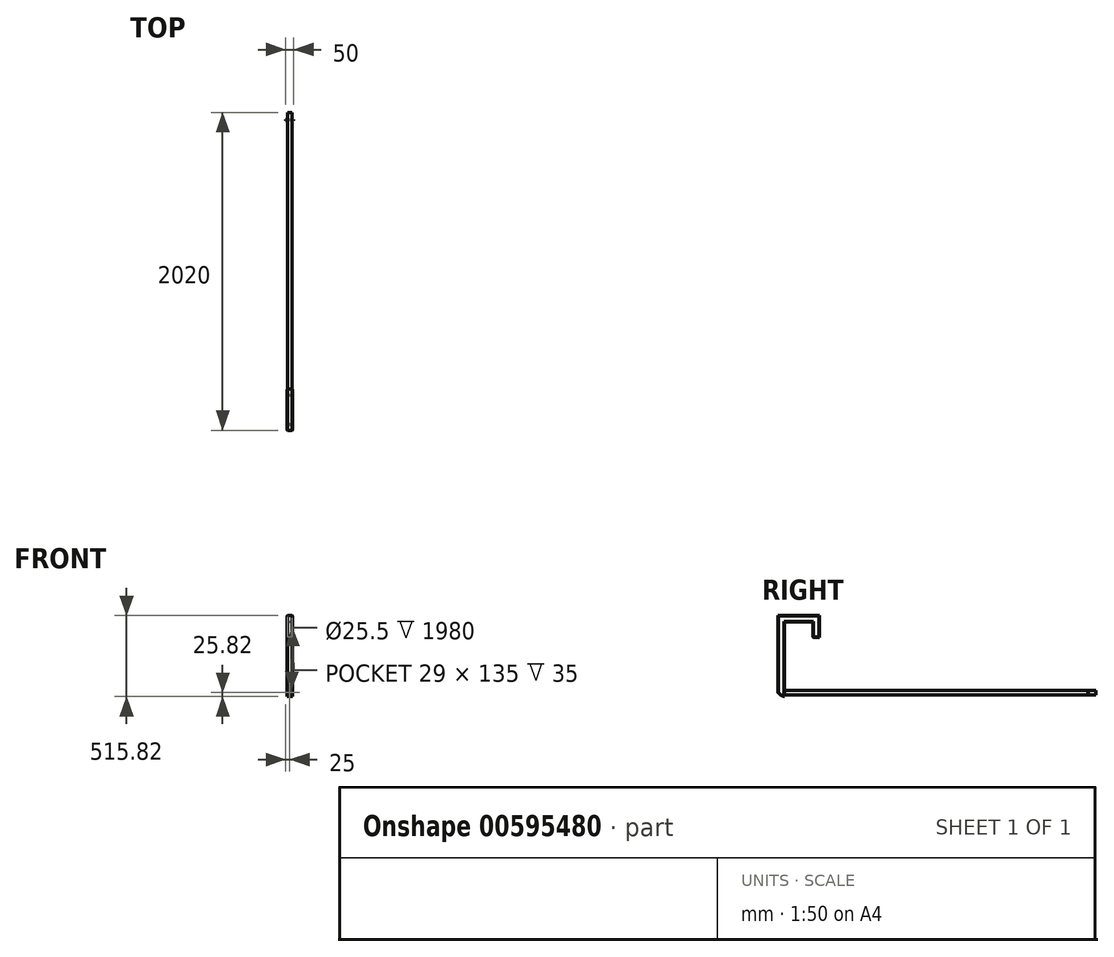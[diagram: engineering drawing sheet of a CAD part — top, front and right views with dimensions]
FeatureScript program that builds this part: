
annotation { "Feature Type Name" : "Feature", "Feature Type Description" : "" }
export const myFeature = defineFeature(function(context is Context, id is Id, definition is map)
    precondition{}
    {
        {
            var Q0;
            Q0=qCreatedBy(makeId("Front.planeOp"),FACE);
            var sketch = newSketch(context, id + "F0", { "sketchPlane" : qUnion([Q0])});
            skCircle(sketch, "E0", {"center": v(0, 0) * mm, "radius": 14 * mm});
            skSolve(sketch);
        }
        {
            var Q0;
            Q0=qCreatedBy(makeId("Front.planeOp"),FACE);
            var sketch = newSketch(context, id + "F1", { "sketchPlane" : qUnion([Q0])});
            skCircle(sketch, "E1", {"center": v(0, 0) * mm, "radius": 12.75 * mm});
            skSolve(sketch);
        }
        {
            var Q0;
            Q0=makeQuery(id+"F0.imprint","IMPRINT",FACE,{"disambiguationData":[TD([[makeQuery(id+"F0.imprint","IMPRINT",EDGE,{"derivedFrom":sQuery(id+"F0.wireOp",EDGE,"E0")}),1.0]])]});
            extrude(context, id + "F2", {"entities" : qUnion([Q0]), "oppositeDirection" : true, "depth" : 2000 * mm, "offsetDistance" : 25 * mm});
        }
        {
            var Q0;
            Q0 = qSketchRegion(id + "F1", true);
            extrude(context, id + "F3", {"entities" : qUnion([Q0]), "operationType" : NewBodyOperationType.REMOVE, "oppositeDirection" : true, "depth" : 2000 * mm, "offsetDistance" : 25 * mm});
        }
        {
            var Q0;
            Q0=qCreatedBy(makeId("Right.planeOp"),FACE);
            cPlane(context, id + "F4", {"entities" : qUnion([Q0]), "cplaneType" : CPlaneType.OFFSET, "offset" : 17 * mm, "width" : 150 * mm, "height" : 150 * mm});
        }
        {
            var Q0;
            Q0=qCreatedBy(id+"F4.planeOp",FACE);
            var sketch = newSketch(context, id + "F5", { "sketchPlane" : qUnion([Q0])});
            skLineSegment(sketch, "E2", {"start": v(-20, 0) * mm, "end": v(-20, 490) * mm});
            skArc(sketch, "E3", {"start": v(-20, 0) * mm, "mid": v(-1.7, -16.2) * mm, "end": v(20, -27.49) * mm});
            skLineSegment(sketch, "E4", {"start": v(20, -27.49) * mm, "end": v(20, 365.4) * mm, "construction": true});
            skLineSegment(sketch, "E5", {"start": v(20, 450) * mm, "end": v(20, -27.49) * mm});
            skLineSegment(sketch, "E6", {"start": v(-20, 490) * mm, "end": v(242.17, 490) * mm});
            skLineSegment(sketch, "E7", {"start": v(20, 450) * mm, "end": v(202.17, 450) * mm});
            skLineSegment(sketch, "E8", {"start": v(242.17, 350) * mm, "end": v(242.17, 490) * mm});
            skLineSegment(sketch, "E9", {"start": v(202.17, 450) * mm, "end": v(202.17, 350) * mm});
            skLineSegment(sketch, "E10", {"start": v(202.17, 350) * mm, "end": v(242.17, 350) * mm});
            skSolve(sketch);
        }
        {
            var Q0;
            Q0 = qSketchRegion(id + "F5", true);
            extrude(context, id + "F6", {"entities" : qUnion([Q0]), "operationType" : NewBodyOperationType.ADD, "oppositeDirection" : true, "depth" : 34 * mm, "offsetDistance" : 25 * mm});
        }
        {
            var Q0;
            Q0=makeQuery(id+"F6.opExtrude","CAP_FACE",FACE,{"disambiguationData":[OSD([sQuery(id+"F5.wireOp",EDGE,"E2"),sQuery(id+"F5.wireOp",EDGE,"E3"),sQuery(id+"F5.wireOp",EDGE,"E5"),sQuery(id+"F5.wireOp",EDGE,"284f362e-461d-4ea2-9a0a-4d998c6a0b75")])],"isStart":true});
            var Q1;
            Q1=makeQuery(id+"F2.opExtrude","SWEPT_BODY",BODY,{"disambiguationData":[OSD([sQuery(id+"F0.wireOp",EDGE,"E0")])]});
            shell(context, id + "F7", {"isHollow" : true, "entities" : qUnion([Q0]), "parts" : qUnion([Q1]), "thickness" : 2.5 * mm});
        }
        {
            var Q0;
            Q0=makeQuery(id+"F6.opExtrude","CAP_FACE",FACE,{"disambiguationData":[OSD([sQuery(id+"F5.wireOp",EDGE,"E2"),sQuery(id+"F5.wireOp",EDGE,"E3"),sQuery(id+"F5.wireOp",EDGE,"E5"),sQuery(id+"F5.wireOp",EDGE,"284f362e-461d-4ea2-9a0a-4d998c6a0b75")])],"isStart":false});
            var Q1;
            Q1=makeQuery(id+"F6.opExtrude","SWEPT_FACE",FACE,{"disambiguationData":[OSD([sQuery(id+"F5.wireOp",EDGE,"284f362e-461d-4ea2-9a0a-4d998c6a0b75")])]});
            var Q2;
            Q2=makeQuery(id+"F6.opExtrude","SWEPT_EDGE",EDGE,{"disambiguationData":[OSD([sQuery(id+"F5.wireOp",EDGE,"E3"),sQuery(id+"F5.wireOp",EDGE,"E5")])]});
            var Q3;
            Q3=makeQuery(id+"F6.opExtrude","CAP_EDGE",EDGE,{"disambiguationData":[OSD([sQuery(id+"F5.wireOp",EDGE,"E5")])],"isStart":true});
            var Q4;
            Q4=makeQuery(id+"F6.opExtrude","CAP_EDGE",EDGE,{"disambiguationData":[OSD([sQuery(id+"F5.wireOp",EDGE,"E2")])],"isStart":true});
            var Q5;
            Q5=makeQuery(id+"F6.opExtrude","CAP_EDGE",EDGE,{"disambiguationData":[OSD([sQuery(id+"F5.wireOp",EDGE,"E8")])],"isStart":true});
            var Q6;
            Q6=makeQuery(id+"F6.opExtrude","CAP_EDGE",EDGE,{"disambiguationData":[OSD([sQuery(id+"F5.wireOp",EDGE,"E7")])],"isStart":true});
            var Q7;
            Q7=makeQuery(id+"F6.opExtrude","SWEPT_EDGE",EDGE,{"disambiguationData":[OSD([sQuery(id+"F5.wireOp",EDGE,"E2"),sQuery(id+"F5.wireOp",EDGE,"E3")])]});
            var Q8;
            Q8=makeQuery(id+"F6.opExtrude","CAP_EDGE",EDGE,{"disambiguationData":[OSD([sQuery(id+"F5.wireOp",EDGE,"E6")])],"isStart":true});
            var Q9;
            Q9=makeQuery(id+"F6.opExtrude","CAP_EDGE",EDGE,{"disambiguationData":[OSD([sQuery(id+"F5.wireOp",EDGE,"E9")])],"isStart":true});
            var Q10;
            Q10=makeQuery(id+"F6.opExtrude","SWEPT_EDGE",EDGE,{"disambiguationData":[OSD([sQuery(id+"F5.wireOp",EDGE,"E9"),sQuery(id+"F5.wireOp",EDGE,"E10")])]});
            var Q11;
            Q11=makeQuery(id+"F6.opExtrude","CAP_EDGE",EDGE,{"disambiguationData":[OSD([sQuery(id+"F5.wireOp",EDGE,"E10")])],"isStart":true});
            var Q12;
            Q12=makeQuery(id+"F6.opExtrude","CAP_EDGE",EDGE,{"disambiguationData":[OSD([sQuery(id+"F5.wireOp",EDGE,"E3")])],"isStart":true});
            chamfer(context, id + "F8", {"entities" : qUnion([Q0, Q1, Q2, Q3, Q4, Q5, Q6, Q7, Q8, Q9, Q10, Q11, Q12]), "width" : 3 * mm, "tangentPropagation" : true});
        }
        {
            var Q0;
            Q0=qCreatedBy(makeId("Front.planeOp"),FACE);
            cPlane(context, id + "F9", {"entities" : qUnion([Q0]), "cplaneType" : CPlaneType.OFFSET, "offset" : 1950 * mm, "oppositeDirection" : true, "width" : 150 * mm, "height" : 150 * mm});
        }
        {
            var Q0;
            Q0=qCreatedBy(id+"F9.planeOp",FACE);
            var sketch = newSketch(context, id + "F10", { "sketchPlane" : qUnion([Q0])});
            skLineSegment(sketch, "E11", {"start": v(25, 3) * mm, "end": v(-25, 3) * mm});
            skLineSegment(sketch, "E12", {"start": v(-42.05, 0) * mm, "end": v(60.71, 0) * mm, "construction": true});
            skLineSegment(sketch, "E13", {"start": v(25, 3) * mm, "end": v(25, 0) * mm});
            skLineSegment(sketch, "E14", {"start": v(-25, 3) * mm, "end": v(-25, 0) * mm});
            skLineSegment(sketch, "E15", {"start": v(25, 0) * mm, "end": v(-25, 0) * mm});
            skSolve(sketch);
        }
        {
            var Q0;
            Q0 = qSketchRegion(id + "F10", true);
            var Q1;
            Q1=sQuery(id+"F10.wireOp",EDGE,"E12");
            revolve(context, id + "F11", {"operationType" : NewBodyOperationType.ADD, "entities" : qUnion([Q0]), "axis" : qUnion([Q1]), "revolveType" : RevolveType.FULL});
        }
    });
